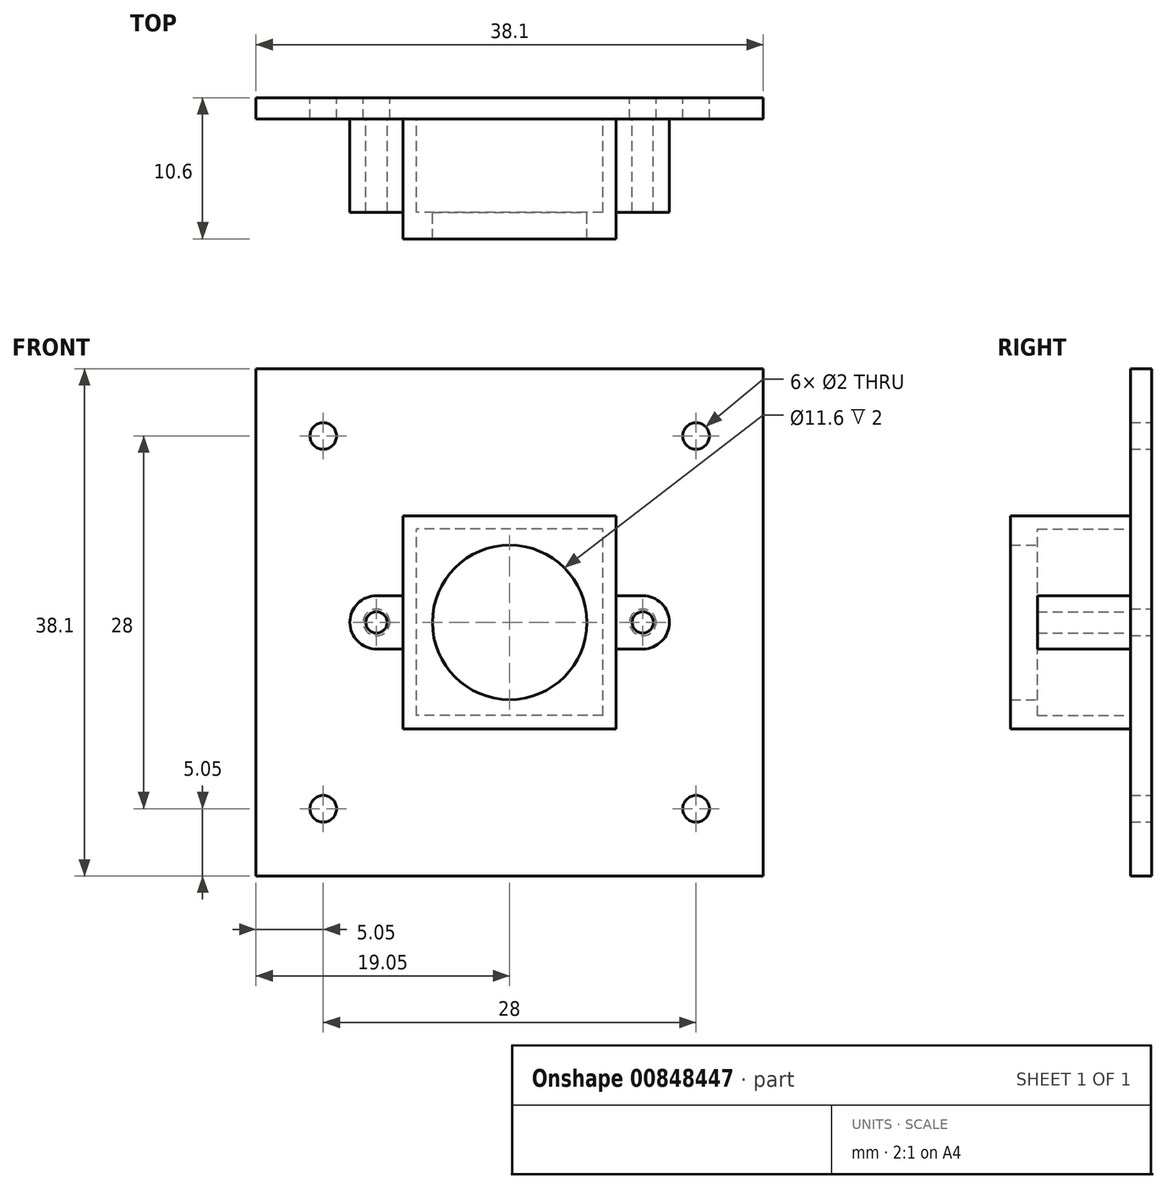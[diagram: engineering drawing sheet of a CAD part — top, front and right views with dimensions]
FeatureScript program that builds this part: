
annotation { "Feature Type Name" : "Feature", "Feature Type Description" : "" }
export const myFeature = defineFeature(function(context is Context, id is Id, definition is map)
    precondition{}
    {
        {
            var Q0;
            Q0=qCreatedBy(makeId("Front.planeOp"),FACE);
            var sketch = newSketch(context, id + "F0", { "sketchPlane" : qUnion([Q0])});
            skLineSegment(sketch, "E0.bottom", {"start": v(19.05, 19.05) * mm, "end": v(-19.05, 19.05) * mm});
            skLineSegment(sketch, "E0.top", {"start": v(19.05, -19.05) * mm, "end": v(-19.05, -19.05) * mm});
            skLineSegment(sketch, "E0.left", {"start": v(19.05, 19.05) * mm, "end": v(19.05, -19.05) * mm});
            skLineSegment(sketch, "E0.right", {"start": v(-19.05, 19.05) * mm, "end": v(-19.05, -19.05) * mm});
            skPoint(sketch, "E0.middle", {"position": v(0, 0) * mm});
            skLineSegment(sketch, "E1.bottom", {"start": v(14, 14) * mm, "end": v(-14, 14) * mm, "construction": true});
            skLineSegment(sketch, "E1.top", {"start": v(14, -14) * mm, "end": v(-14, -14) * mm, "construction": true});
            skLineSegment(sketch, "E1.left", {"start": v(14, 14) * mm, "end": v(14, -14) * mm, "construction": true});
            skLineSegment(sketch, "E1.right", {"start": v(-14, 14) * mm, "end": v(-14, -14) * mm, "construction": true});
            skCircle(sketch, "E2", {"center": v(14, 14) * mm, "radius": 1 * mm});
            skCircle(sketch, "E3", {"center": v(-14, 14) * mm, "radius": 1 * mm});
            skCircle(sketch, "E4", {"center": v(-14, -14) * mm, "radius": 1 * mm});
            skCircle(sketch, "E5", {"center": v(14, -14) * mm, "radius": 1 * mm});
            skLineSegment(sketch, "E6", {"start": v(-28.1, 0) * mm, "end": v(33.58, 0) * mm, "construction": true});
            skLineSegment(sketch, "E7", {"start": v(0, 29.08) * mm, "end": v(0, -28.27) * mm, "construction": true});
            skPoint(sketch, "E7.endSnap0", {"position": v(0, -14) * mm});
            skCircle(sketch, "E8", {"center": v(-10, 0) * mm, "radius": 1 * mm});
            skCircle(sketch, "E9", {"center": v(10, 0) * mm, "radius": 1 * mm});
            skSolve(sketch);
        }
        {
            var Q0;
            Q0=makeQuery(id+"F0.imprint","IMPRINT",FACE,{"disambiguationData":[TD([[makeQuery(id+"F0.imprint","IMPRINT",EDGE,{"derivedFrom":sQuery(id+"F0.wireOp",EDGE,"E0.bottom")}),1.0]])]});
            extrude(context, id + "F1", {"entities" : qUnion([Q0]), "depth" : 1.6 * mm, "offsetDistance" : 25 * mm});
        }
        {
            var Q0;
            Q0=makeQuery(id+"F1.opExtrude","CAP_FACE",FACE,{"disambiguationData":[OSD([sQuery(id+"F0.wireOp",EDGE,"E0.bottom"),sQuery(id+"F0.wireOp",EDGE,"E0.top"),sQuery(id+"F0.wireOp",EDGE,"E0.left"),sQuery(id+"F0.wireOp",EDGE,"E0.right"),sQuery(id+"F0.wireOp",EDGE,"E2"),sQuery(id+"F0.wireOp",EDGE,"E3"),sQuery(id+"F0.wireOp",EDGE,"E4"),sQuery(id+"F0.wireOp",EDGE,"E5"),sQuery(id+"F0.wireOp",EDGE,"E8"),sQuery(id+"F0.wireOp",EDGE,"E9")])],"isStart":false});
            var sketch = newSketch(context, id + "F2", { "sketchPlane" : qUnion([Q0])});
            skLineSegment(sketch, "E10.bottom", {"start": v(8, -8) * mm, "end": v(-8, -8) * mm});
            skLineSegment(sketch, "E10.top", {"start": v(8, 8) * mm, "end": v(-8, 8) * mm});
            skLineSegment(sketch, "E10.left", {"start": v(8, -8) * mm, "end": v(8, -2) * mm});
            skLineSegment(sketch, "E10.right", {"start": v(-8, -8) * mm, "end": v(-8, -2) * mm});
            skPoint(sketch, "E10.middle", {"position": v(0, 0) * mm});
            skArc(sketch, "E11", {"start": v(-10, 2) * mm, "mid": v(-12, 0) * mm, "end": v(-10, -2) * mm});
            skArc(sketch, "E12", {"start": v(10, -2) * mm, "mid": v(12, 0) * mm, "end": v(10, 2) * mm});
            skLineSegment(sketch, "E13.0", {"start": v(7, 7) * mm, "end": v(-7, 7) * mm});
            skLineSegment(sketch, "E13.1", {"start": v(7, -7) * mm, "end": v(7, 7) * mm});
            skLineSegment(sketch, "E13.2", {"start": v(7, -7) * mm, "end": v(-7, -7) * mm});
            skLineSegment(sketch, "E13.3", {"start": v(-7, -7) * mm, "end": v(-7, 7) * mm});
            skLineSegment(sketch, "E14", {"start": v(-10, 2) * mm, "end": v(-8, 2) * mm});
            skLineSegment(sketch, "E15", {"start": v(-10, -2) * mm, "end": v(-8, -2) * mm});
            skLineSegment(sketch, "E16", {"start": v(8, -2) * mm, "end": v(10, -2) * mm});
            skLineSegment(sketch, "E17.trimOffspring", {"start": v(8, 2) * mm, "end": v(10, 2) * mm});
            skLineSegment(sketch, "E18.trimOffspring", {"start": v(8, 2) * mm, "end": v(8, 8) * mm});
            skLineSegment(sketch, "E19.trimOffspring", {"start": v(-8, 2) * mm, "end": v(-8, 8) * mm});
            skCircle(sketch, "E20", {"center": v(-10, 0) * mm, "radius": 0.8 * mm});
            skCircle(sketch, "E21", {"center": v(10, 0) * mm, "radius": 0.8 * mm});
            skSolve(sketch);
        }
        {
            var Q0;
            Q0 = qSketchRegion(id + "F2", true);
            extrude(context, id + "F3", {"entities" : qUnion([Q0]), "depth" : 7 * mm, "offsetDistance" : 25 * mm});
        }
        {
            var Q0;
            Q0=makeQuery(id+"F3.opExtrude","CAP_FACE",FACE,{"disambiguationData":[OSD([sQuery(id+"F2.wireOp",EDGE,"E10.bottom"),sQuery(id+"F2.wireOp",EDGE,"E10.top"),sQuery(id+"F2.wireOp",EDGE,"E10.left"),sQuery(id+"F2.wireOp",EDGE,"E10.right"),sQuery(id+"F2.wireOp",EDGE,"E11"),sQuery(id+"F2.wireOp",EDGE,"E12"),sQuery(id+"F2.wireOp",EDGE,"E13.0"),sQuery(id+"F2.wireOp",EDGE,"E13.1"),sQuery(id+"F2.wireOp",EDGE,"E13.2"),sQuery(id+"F2.wireOp",EDGE,"E13.3"),sQuery(id+"F2.wireOp",EDGE,"E14"),sQuery(id+"F2.wireOp",EDGE,"E15"),sQuery(id+"F2.wireOp",EDGE,"E16"),sQuery(id+"F2.wireOp",EDGE,"E17.trimOffspring"),sQuery(id+"F2.wireOp",EDGE,"E18.trimOffspring"),sQuery(id+"F2.wireOp",EDGE,"E19.trimOffspring"),sQuery(id+"F2.wireOp",EDGE,"E20"),sQuery(id+"F2.wireOp",EDGE,"E21")])],"isStart":false});
            var sketch = newSketch(context, id + "F4", { "sketchPlane" : qUnion([Q0])});
            skLineSegment(sketch, "E22.bottom", {"start": v(-8, 8) * mm, "end": v(8, 8) * mm});
            skLineSegment(sketch, "E22.top", {"start": v(-8, -8) * mm, "end": v(8, -8) * mm});
            skLineSegment(sketch, "E22.left", {"start": v(-8, 8) * mm, "end": v(-8, -8) * mm});
            skLineSegment(sketch, "E22.right", {"start": v(8, 8) * mm, "end": v(8, -8) * mm});
            skCircle(sketch, "E23", {"center": v(0, 0) * mm, "radius": 5.8 * mm});
            skSolve(sketch);
        }
        {
            var Q0;
            Q0 = qSketchRegion(id + "F4", true);
            extrude(context, id + "F5", {"entities" : qUnion([Q0]), "operationType" : NewBodyOperationType.ADD, "depth" : 2 * mm, "offsetDistance" : 25 * mm});
        }
    });
